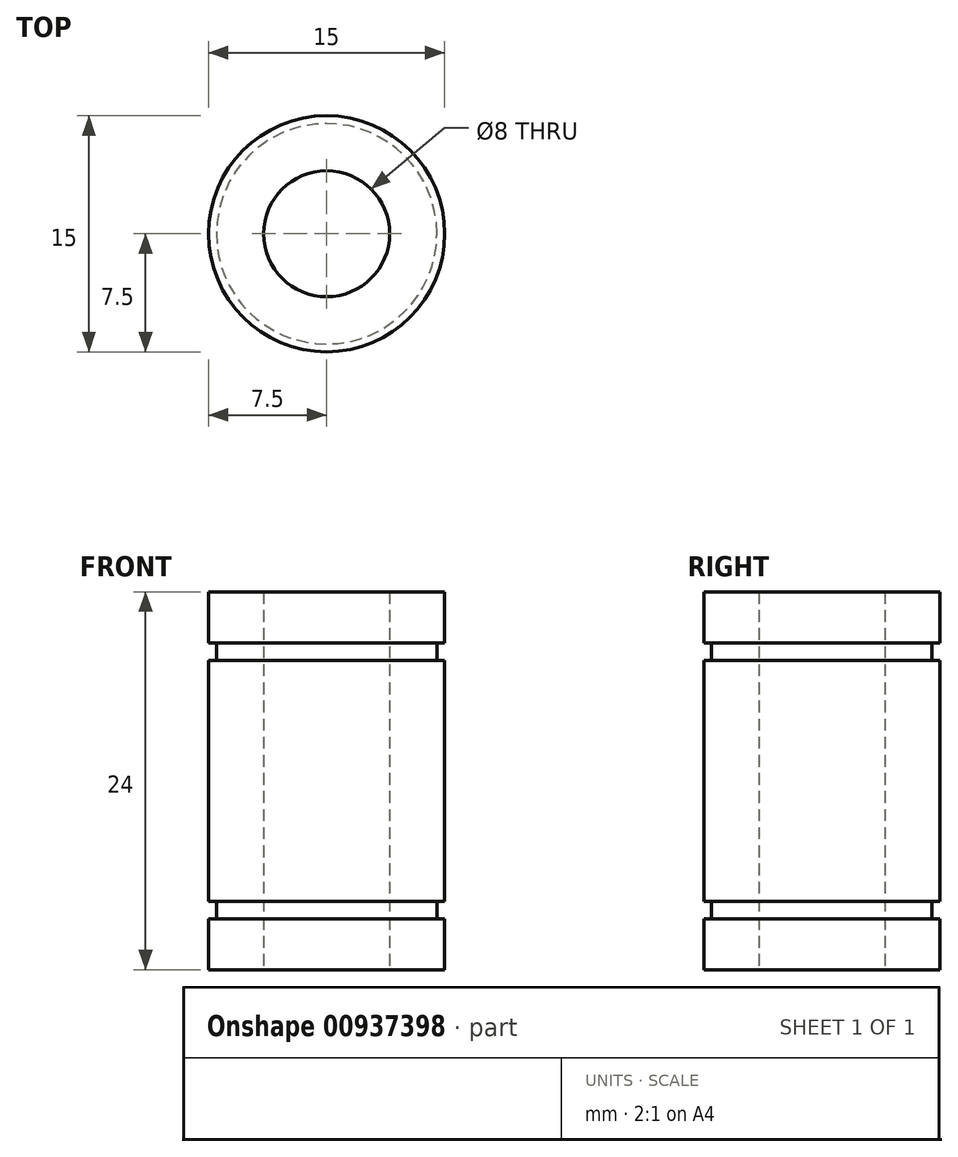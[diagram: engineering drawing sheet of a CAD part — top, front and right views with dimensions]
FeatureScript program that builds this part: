
annotation { "Feature Type Name" : "Feature", "Feature Type Description" : "" }
export const myFeature = defineFeature(function(context is Context, id is Id, definition is map)
    precondition{}
    {
        {
            var Q0;
            Q0=qCreatedBy(makeId("Top.planeOp"),FACE);
            var sketch = newSketch(context, id + "F0", { "sketchPlane" : qUnion([Q0])});
            skCircle(sketch, "E0", {"center": v(0, 0) * mm, "radius": 7.5 * mm});
            skCircle(sketch, "E1", {"center": v(0, 0) * mm, "radius": 4 * mm});
            skSolve(sketch);
        }
        {
            var Q0;
            Q0 = qSketchRegion(id + "F0", true);
            extrude(context, id + "F1", {"entities" : qUnion([Q0]), "depth" : 24 * mm, "offsetDistance" : 25 * mm});
        }
        {
            var Q0;
            Q0=qCreatedBy(makeId("Right.planeOp"),FACE);
            var sketch = newSketch(context, id + "F2", { "sketchPlane" : qUnion([Q0])});
            skLineSegment(sketch, "E2.bottom", {"start": v(7, 3.25) * mm, "end": v(7.5, 3.25) * mm});
            skLineSegment(sketch, "E2.top", {"start": v(7, 4.35) * mm, "end": v(7.5, 4.35) * mm});
            skLineSegment(sketch, "E2.left", {"start": v(7, 3.25) * mm, "end": v(7, 4.35) * mm});
            skLineSegment(sketch, "E2.right", {"start": v(7.5, 3.25) * mm, "end": v(7.5, 4.35) * mm});
            skLineSegment(sketch, "E3.bottom", {"start": v(7, 19.65) * mm, "end": v(7.5, 19.65) * mm});
            skLineSegment(sketch, "E3.top", {"start": v(7, 20.75) * mm, "end": v(7.5, 20.75) * mm});
            skLineSegment(sketch, "E3.left", {"start": v(7, 19.65) * mm, "end": v(7, 20.75) * mm});
            skLineSegment(sketch, "E3.right", {"start": v(7.5, 19.65) * mm, "end": v(7.5, 20.75) * mm});
            skSolve(sketch);
        }
        {
            var Q0;
            Q0 = qSketchRegion(id + "F2", true);
            var Q1;
            Q1=makeQuery(id+"F1.opExtrude","SWEPT_FACE",FACE,{"disambiguationData":[OSD([sQuery(id+"F0.wireOp",EDGE,"E0")])]});
            revolve(context, id + "F3", {"operationType" : NewBodyOperationType.REMOVE, "surfaceOperationType" : NewSurfaceOperationType.NEW, "entities" : qUnion([Q0]), "axis" : qUnion([Q1]), "revolveType" : RevolveType.FULL, "oppositeDirection" : true});
        }
    });
